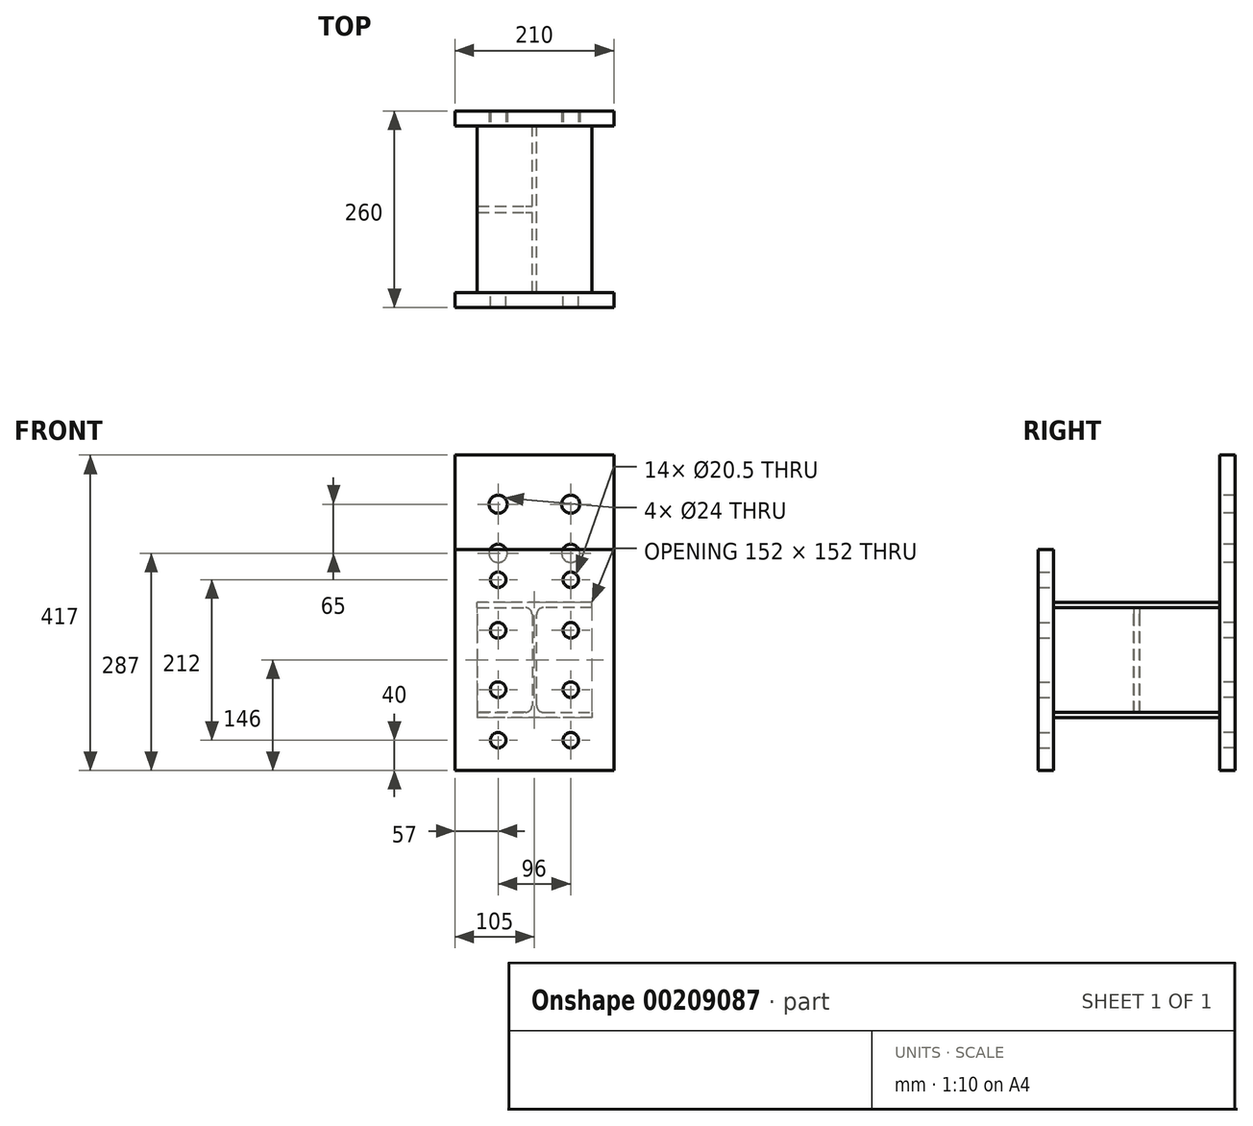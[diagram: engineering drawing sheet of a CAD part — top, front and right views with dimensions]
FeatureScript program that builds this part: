
annotation { "Feature Type Name" : "Feature", "Feature Type Description" : "" }
export const myFeature = defineFeature(function(context is Context, id is Id, definition is map)
    precondition{}
    {
        {
            var Q0;
            Q0=qCreatedBy(makeId("Front.planeOp"),FACE);
            var sketch = newSketch(context, id + "F0", { "sketchPlane" : qUnion([Q0])});
            skLineSegment(sketch, "E0.left", {"start": v(3.05, -60.3) * mm, "end": v(3.05, 60.3) * mm});
            skLineSegment(sketch, "E0.right", {"start": v(-3.05, -60.3) * mm, "end": v(-3.05, 60.3) * mm});
            skPoint(sketch, "E0.middle", {"position": v(0, 0) * mm});
            skLineSegment(sketch, "E1.bottom", {"start": v(76, 69.2) * mm, "end": v(11.95, 69.2) * mm});
            skLineSegment(sketch, "E1.top", {"start": v(76, 76) * mm, "end": v(-76, 76) * mm});
            skLineSegment(sketch, "E1.left", {"start": v(76, 69.2) * mm, "end": v(76, 76) * mm});
            skLineSegment(sketch, "E1.right", {"start": v(-76, 69.2) * mm, "end": v(-76, 76) * mm});
            skLineSegment(sketch, "E2.bottom", {"start": v(-11.95, -69.2) * mm, "end": v(-76, -69.2) * mm});
            skLineSegment(sketch, "E2.top", {"start": v(76, -76) * mm, "end": v(-76, -76) * mm});
            skLineSegment(sketch, "E2.left", {"start": v(76, -69.2) * mm, "end": v(76, -76) * mm});
            skLineSegment(sketch, "E2.right", {"start": v(-76, -69.2) * mm, "end": v(-76, -76) * mm});
            skPoint(sketch, "E3.newPointB", {"position": v(-76, 69.2) * mm});
            skArc(sketch, "E3.filletArc", {"start": v(11.95, 69.2) * mm, "mid": v(5.66, 66.6) * mm, "end": v(3.05, 60.3) * mm});
            skLineSegment(sketch, "E4", {"start": v(-76, 69.2) * mm, "end": v(-11.95, 69.2) * mm});
            skArc(sketch, "E5.filletArc", {"start": v(-3.05, 60.3) * mm, "mid": v(-5.66, 66.6) * mm, "end": v(-11.95, 69.2) * mm});
            skPoint(sketch, "E6.newPointA", {"position": v(76, -69.2) * mm});
            skArc(sketch, "E6.filletArc", {"start": v(-11.95, -69.2) * mm, "mid": v(-5.66, -66.6) * mm, "end": v(-3.05, -60.3) * mm});
            skLineSegment(sketch, "E7", {"start": v(11.95, -69.2) * mm, "end": v(76, -69.2) * mm});
            skArc(sketch, "E8.filletArc", {"start": v(3.05, -60.3) * mm, "mid": v(5.66, -66.6) * mm, "end": v(11.95, -69.2) * mm});
            skSolve(sketch);
        }
        {
            var Q0;
            Q0=qSketchRegion(id+"F0",true);
            extrude(context, id + "F1", {"entities" : qUnion([Q0]), "depth" : 220 * mm, "symmetric" : true});
        }
        {
            var Q0;
            Q0=makeQuery(id+"F1.opExtrude","SWEPT_FACE",FACE,{"disambiguationData":[OSD([sQuery(id+"F0.wireOp",EDGE,"E0.left")])]});
            var sketch = newSketch(context, id + "F2", { "sketchPlane" : qUnion([Q0])});
            skLineSegment(sketch, "E9.bottom", {"start": v(4, -69.2) * mm, "end": v(-4, -69.2) * mm});
            skLineSegment(sketch, "E9.top", {"start": v(4, 69.2) * mm, "end": v(-4, 69.2) * mm});
            skLineSegment(sketch, "E9.left", {"start": v(4, -69.2) * mm, "end": v(4, 69.2) * mm});
            skLineSegment(sketch, "E9.right", {"start": v(-4, -69.2) * mm, "end": v(-4, 69.2) * mm});
            skPoint(sketch, "E9.middle", {"position": v(0, 0) * mm});
            skSolve(sketch);
        }
        {
            var Q0;
            Q0=qSketchRegion(id+"F2",true);
            extrude(context, id + "F3", {"entities" : qUnion([Q0]), "operationType" : NewBodyOperationType.ADD, "oppositeDirection" : true, "depth" : 78.1 * mm});
        }
        {
            var Q0;
            Q0=makeQuery(id+"F1.opExtrude","CAP_FACE",FACE,{"disambiguationData":[OSD([sQuery(id+"F0.wireOp",EDGE,"E0.left"),sQuery(id+"F0.wireOp",EDGE,"E0.right"),sQuery(id+"F0.wireOp",EDGE,"E1.bottom"),sQuery(id+"F0.wireOp",EDGE,"E1.top"),sQuery(id+"F0.wireOp",EDGE,"E1.left"),sQuery(id+"F0.wireOp",EDGE,"E1.right"),sQuery(id+"F0.wireOp",EDGE,"E2.bottom"),sQuery(id+"F0.wireOp",EDGE,"E2.top"),sQuery(id+"F0.wireOp",EDGE,"E2.left"),sQuery(id+"F0.wireOp",EDGE,"E2.right"),sQuery(id+"F0.wireOp",EDGE,"E3.filletArc"),sQuery(id+"F0.wireOp",EDGE,"E4"),sQuery(id+"F0.wireOp",EDGE,"E5.filletArc"),sQuery(id+"F0.wireOp",EDGE,"E6.filletArc"),sQuery(id+"F0.wireOp",EDGE,"E7"),sQuery(id+"F0.wireOp",EDGE,"E8.filletArc")])],"isStart":false});
            var sketch = newSketch(context, id + "F4", { "sketchPlane" : qUnion([Q0])});
            skLineSegment(sketch, "E10.bottom", {"start": v(105, -146) * mm, "end": v(-105, -146) * mm});
            skLineSegment(sketch, "E10.top", {"start": v(105, 146) * mm, "end": v(-105, 146) * mm});
            skLineSegment(sketch, "E10.left", {"start": v(105, -146) * mm, "end": v(105, 146) * mm});
            skLineSegment(sketch, "E10.right", {"start": v(-105, -146) * mm, "end": v(-105, 146) * mm});
            skPoint(sketch, "E10.middle", {"position": v(0, 0) * mm});
            skCircle(sketch, "E11", {"center": v(-48, 106) * mm, "radius": 10.25 * mm});
            skCircle(sketch, "E12", {"center": v(-48, 39.2) * mm, "radius": 10.25 * mm});
            skCircle(sketch, "E13", {"center": v(-48, -39.2) * mm, "radius": 10.25 * mm});
            skCircle(sketch, "E14", {"center": v(-48, -106) * mm, "radius": 10.25 * mm});
            skCircle(sketch, "E15.MirrorC", {"center": v(48, -39.2) * mm, "radius": 10.25 * mm});
            skCircle(sketch, "E16.MirrorC", {"center": v(48, 39.2) * mm, "radius": 10.25 * mm});
            skCircle(sketch, "E17.MirrorC", {"center": v(48, -106) * mm, "radius": 10.25 * mm});
            skCircle(sketch, "E18.MirrorC", {"center": v(48, 106) * mm, "radius": 10.25 * mm});
            skSolve(sketch);
        }
        {
            var Q0;
            Q0=qSketchRegion(id+"F4",true);
            extrude(context, id + "F5", {"entities" : qUnion([Q0]), "operationType" : NewBodyOperationType.ADD, "depth" : 20 * mm});
        }
        {
            var Q0;
            Q0=makeQuery(id+"F1.opExtrude","CAP_FACE",FACE,{"disambiguationData":[OSD([sQuery(id+"F0.wireOp",EDGE,"E0.left"),sQuery(id+"F0.wireOp",EDGE,"E0.right"),sQuery(id+"F0.wireOp",EDGE,"E1.bottom"),sQuery(id+"F0.wireOp",EDGE,"E1.top"),sQuery(id+"F0.wireOp",EDGE,"E1.left"),sQuery(id+"F0.wireOp",EDGE,"E1.right"),sQuery(id+"F0.wireOp",EDGE,"E2.bottom"),sQuery(id+"F0.wireOp",EDGE,"E2.top"),sQuery(id+"F0.wireOp",EDGE,"E2.left"),sQuery(id+"F0.wireOp",EDGE,"E2.right"),sQuery(id+"F0.wireOp",EDGE,"E3.filletArc"),sQuery(id+"F0.wireOp",EDGE,"E4"),sQuery(id+"F0.wireOp",EDGE,"E5.filletArc"),sQuery(id+"F0.wireOp",EDGE,"E6.filletArc"),sQuery(id+"F0.wireOp",EDGE,"E7"),sQuery(id+"F0.wireOp",EDGE,"E8.filletArc")])],"isStart":true});
            var sketch = newSketch(context, id + "F6", { "sketchPlane" : qUnion([Q0])});
            skLineSegment(sketch, "E19.bottom", {"start": v(-105, -146) * mm, "end": v(105, -146) * mm});
            skLineSegment(sketch, "E19.top", {"start": v(-105, 271) * mm, "end": v(105, 271) * mm});
            skLineSegment(sketch, "E19.left", {"start": v(-105, -146) * mm, "end": v(-105, 271) * mm});
            skLineSegment(sketch, "E19.right", {"start": v(105, 271) * mm, "end": v(105, -146) * mm});
            skCircle(sketch, "E20", {"center": v(-48, 39.2) * mm, "radius": 10.25 * mm});
            skCircle(sketch, "E21.MirrorC", {"center": v(-48, -106) * mm, "radius": 10.25 * mm});
            skCircle(sketch, "E22.MirrorC", {"center": v(-48, -39.2) * mm, "radius": 10.25 * mm});
            skLineSegment(sketch, "E23", {"start": v(0, 0) * mm, "end": v(0, 68.37) * mm});
            skPoint(sketch, "E23.endSnap0", {"position": v(0, 76) * mm});
            skCircle(sketch, "E24.MirrorC", {"center": v(48, -106) * mm, "radius": 10.25 * mm});
            skCircle(sketch, "E25.MirrorC", {"center": v(48, -39.2) * mm, "radius": 10.25 * mm});
            skCircle(sketch, "E26.MirrorC", {"center": v(48, 39.2) * mm, "radius": 10.25 * mm});
            skCircle(sketch, "E27", {"center": v(-48, 141) * mm, "radius": 12 * mm});
            skCircle(sketch, "E28", {"center": v(-48, 206) * mm, "radius": 12 * mm});
            skCircle(sketch, "E29.MirrorC", {"center": v(48, 141) * mm, "radius": 12 * mm});
            skCircle(sketch, "E30.MirrorC", {"center": v(48, 206) * mm, "radius": 12 * mm});
            skSolve(sketch);
        }
        {
            var Q0;
            Q0=qSketchRegion(id+"F6",true);
            extrude(context, id + "F7", {"entities" : qUnion([Q0]), "operationType" : NewBodyOperationType.ADD, "depth" : 20 * mm});
        }
    });
